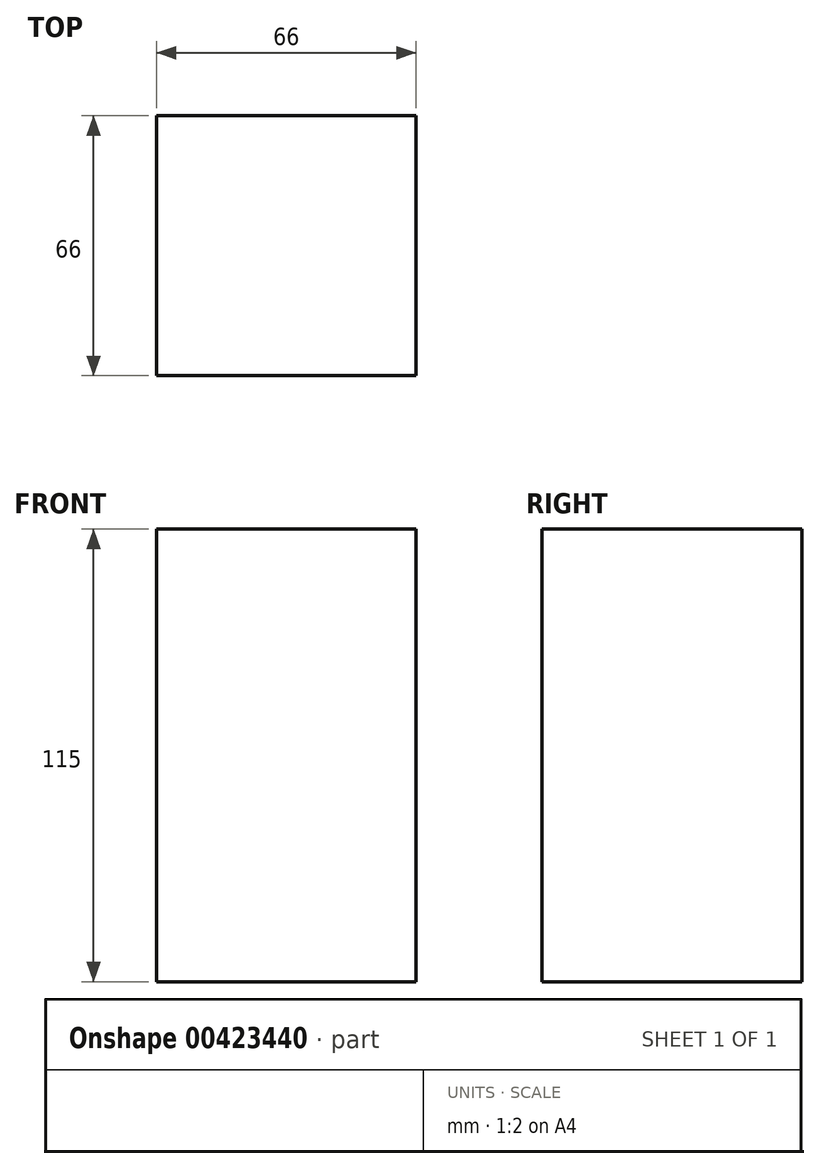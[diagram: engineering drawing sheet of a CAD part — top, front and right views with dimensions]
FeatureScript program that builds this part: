
annotation { "Feature Type Name" : "Feature", "Feature Type Description" : "" }
export const myFeature = defineFeature(function(context is Context, id is Id, definition is map)
    precondition{}
    {
        {
            var Q0;
            Q0=qCreatedBy(makeId("Front.planeOp"),FACE);
            var sketch = newSketch(context, id + "F0", { "sketchPlane" : qUnion([Q0])});
            skLineSegment(sketch, "E0.bottom", {"start": v(-29.86, 68.51) * mm, "end": v(36.14, 68.51) * mm});
            skLineSegment(sketch, "E0.top", {"start": v(-29.86, -46.49) * mm, "end": v(36.14, -46.49) * mm});
            skLineSegment(sketch, "E0.left", {"start": v(-29.86, 68.51) * mm, "end": v(-29.86, -46.49) * mm});
            skLineSegment(sketch, "E0.right", {"start": v(36.14, 68.51) * mm, "end": v(36.14, -46.49) * mm});
            skSolve(sketch);
        }
        {
            var Q0;
            Q0 = qSketchRegion(id + "F0", true);
            extrude(context, id + "F1", {"entities" : qUnion([Q0]), "depth" : 66 * mm});
        }
    });
